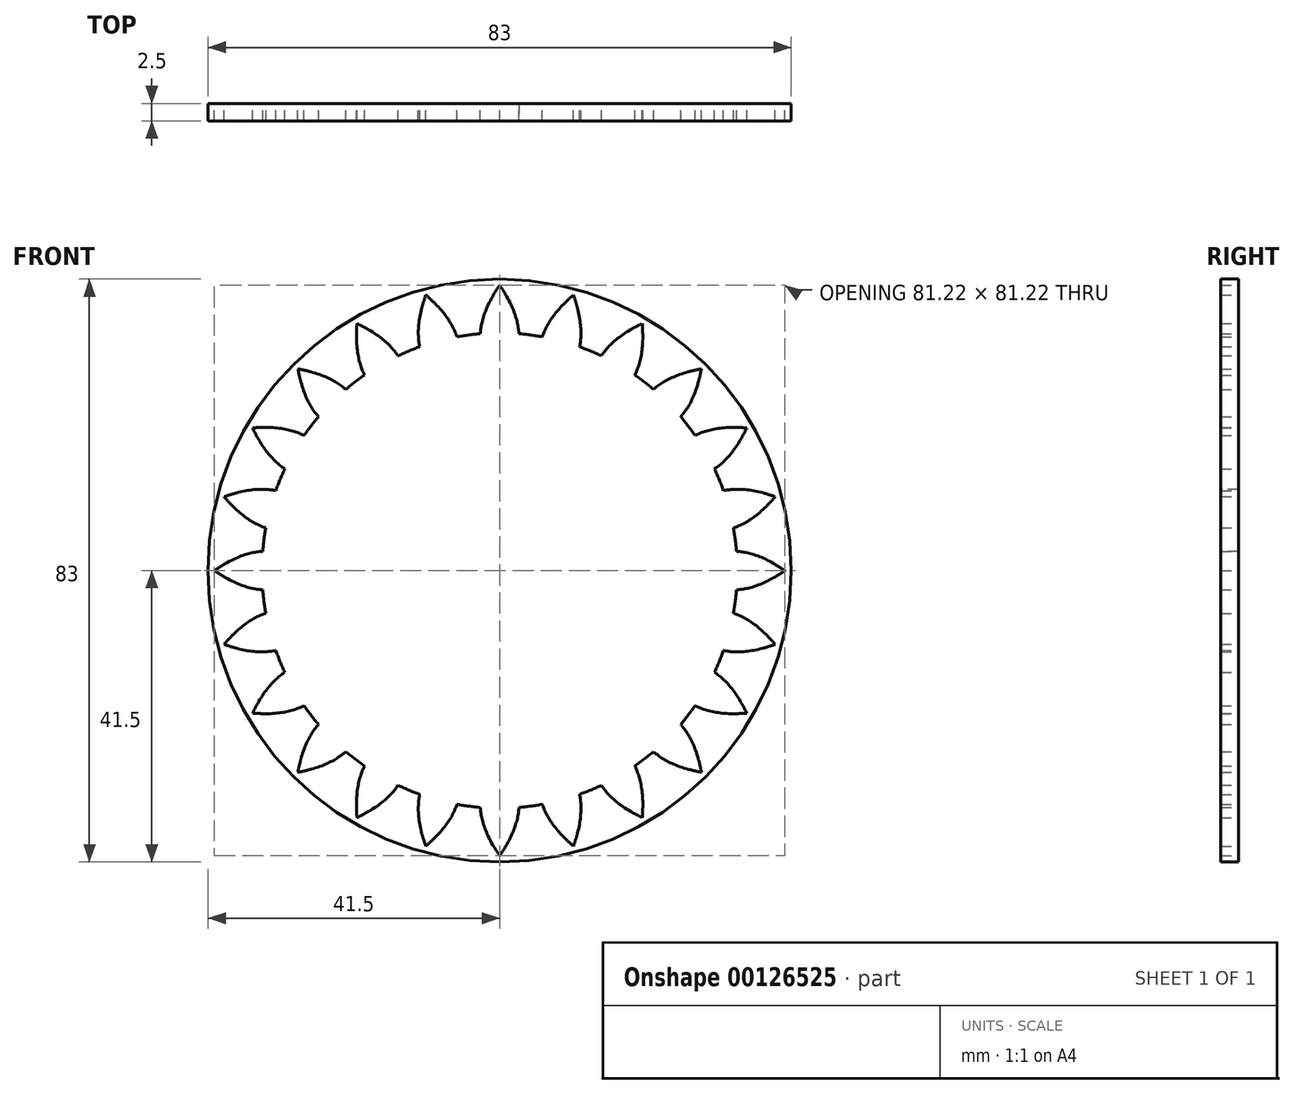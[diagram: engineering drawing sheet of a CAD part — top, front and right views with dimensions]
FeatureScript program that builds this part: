
annotation { "Feature Type Name" : "Feature", "Feature Type Description" : "" }
export const myFeature = defineFeature(function(context is Context, id is Id, definition is map)
    precondition{}
    {
        {
            assignVariable(context, id + "F0", {"name" : "NumberOfTeeth", "anyValue" : 24});
        }
        {
            var Q0;
            Q0=qCreatedBy(makeId("Front.planeOp"),FACE);
            var sketch = newSketch(context, id + "F1", { "sketchPlane" : qUnion([Q0])});
            skCircle(sketch, "E0", {"center": v(0, 0) * mm, "radius": 33.83 * mm});
            skCircle(sketch, "E1", {"center": v(0, 0) * mm, "radius": 39 * mm, "construction": true});
            skCircle(sketch, "E2", {"center": v(0, 0) * mm, "radius": 41.5 * mm});
            skSolve(sketch);
        }
        {
            var Q0;
            Q0=qSketchRegion(id+"F1",true);
            extrude(context, id + "F2", {"entities" : qUnion([Q0]), "depth" : 2.5 * mm});
        }
        {
            var Q0;
            Q0=qCreatedBy(makeId("Front.planeOp"),FACE);
            var sketch = newSketch(context, id + "F3", { "sketchPlane" : qUnion([Q0])});
            skCircle(sketch, "E3", {"center": v(0, 0) * mm, "radius": 36 * mm, "construction": true});
            skLineSegment(sketch, "E4", {"start": v(0, 0) * mm, "end": v(2.35, 35.92) * mm, "construction": true});
            skCircle(sketch, "E5.0", {"center": v(0, 0) * mm, "radius": 33.83 * mm, "construction": true});
            skLineSegment(sketch, "E6", {"start": v(0, 0) * mm, "end": v(4.7, 35.7) * mm, "construction": true});
            skLineSegment(sketch, "E7", {"start": v(0, 0) * mm, "end": v(2.74, 33.72) * mm, "construction": true});
            skLineSegment(sketch, "E8", {"start": v(0, 0) * mm, "end": v(-6.25, 33.25) * mm, "construction": true});
            skLineSegment(sketch, "E9", {"start": v(0, 0) * mm, "end": v(-14.8, 30.42) * mm, "construction": true});
            skLineSegment(sketch, "E10", {"start": v(0, 0) * mm, "end": v(-22.3, 25.45) * mm, "construction": true});
            skLineSegment(sketch, "E11", {"start": v(0, 0) * mm, "end": v(-28.21, 18.67) * mm, "construction": true});
            skLineSegment(sketch, "E12", {"start": v(2.74, 33.72) * mm, "end": v(-6.25, 33.25) * mm, "construction": true});
            skLineSegment(sketch, "E13", {"start": v(-6.25, 33.25) * mm, "end": v(-14.8, 30.42) * mm, "construction": true});
            skLineSegment(sketch, "E14", {"start": v(-14.8, 30.42) * mm, "end": v(-22.3, 25.45) * mm, "construction": true});
            skLineSegment(sketch, "E15", {"start": v(-22.3, 25.45) * mm, "end": v(-28.21, 18.67) * mm, "construction": true});
            skLineSegment(sketch, "E16", {"start": v(0, 0) * mm, "end": v(-32.14, 10.57) * mm, "construction": true});
            skLineSegment(sketch, "E17", {"start": v(-28.21, 18.67) * mm, "end": v(-32.14, 10.57) * mm, "construction": true});
            skLineSegment(sketch, "E18", {"start": v(-6.25, 33.25) * mm, "end": v(2.6, 34.9) * mm, "construction": true});
            skLineSegment(sketch, "E19", {"start": v(-14.8, 30.42) * mm, "end": v(1.4, 38.3) * mm, "construction": true});
            skLineSegment(sketch, "E20", {"start": v(-22.3, 25.45) * mm, "end": v(-1.98, 43.24) * mm, "construction": true});
            skLineSegment(sketch, "E21", {"start": v(-28.21, 18.67) * mm, "end": v(-8.34, 48.7) * mm, "construction": true});
            skLineSegment(sketch, "E22", {"start": v(-32.14, 10.57) * mm, "end": v(-18.08, 53.32) * mm, "construction": true});
            skCircle(sketch, "E23", {"center": v(0, 0) * mm, "radius": 39 * mm, "construction": true});
            skFitSpline(sketch, "E24", {"points": [v(2.74, 33.72) * mm, v(2.6, 34.9) * mm, v(1.4, 38.3) * mm, v(-1.98, 43.24) * mm, v(-8.34, 48.7) * mm, v(-18.08, 53.32) * mm], "startDerivative": vector(0.18, 3.1) * mm, "endDerivative": vector(-9.58, 5.23) * mm});
            skFitSpline(sketch, "E25.MirrorCS", {"points": [v(-2.74, 33.72) * mm, v(-2.6, 34.9) * mm, v(-1.4, 38.3) * mm, v(1.98, 43.24) * mm, v(8.34, 48.7) * mm, v(18.08, 53.32) * mm], "startDerivative": vector(-0.18, 3.1) * mm, "endDerivative": vector(9.58, 5.23) * mm});
            skLineSegment(sketch, "E26", {"start": v(-1.02, 38.99) * mm, "end": v(1, 39.04) * mm});
            skLineSegment(sketch, "E27", {"start": v(-2.74, 33.72) * mm, "end": v(0, 0) * mm});
            skLineSegment(sketch, "E28", {"start": v(2.74, 33.72) * mm, "end": v(0, 0) * mm});
            skSolve(sketch);
        }
        {
            var Q0;
            Q0=qSketchRegion(id+"F3",true);
            extrude(context, id + "F4", {"entities" : qUnion([Q0]), "depth" : 2.5 * mm});
        }
        {
            var Q0;
            Q0=makeQuery(id+"F4.opExtrude","SWEPT_BODY",BODY,{"disambiguationData":[OSD([sQuery(id+"F3.wireOp",EDGE,"E24"),sQuery(id+"F3.wireOp",EDGE,"E25.MirrorCS"),sQuery(id+"F3.wireOp",EDGE,"E26"),sQuery(id+"F3.wireOp",EDGE,"E27"),sQuery(id+"F3.wireOp",EDGE,"E28")])]});
            var Q1;
            Q1=sQuery(id+"F1.wireOp",EDGE,"E0");
            circularPattern(context, id + "F5", {"operationType" : NewBodyOperationType.REMOVE, "entities" : qUnion([Q0]), "axis" : qUnion([Q1]), "angle" : 360 * degree, "instanceCount" : round(getVariable(context, 'NumberOfTeeth')), "equalSpace" : true});
        }
        {
            var Q0;
            {var subQ0=makeQuery(id+"F4.opExtrude","CAP_FACE",FACE,{"disambiguationData":[OSD([sQuery(id+"F3.wireOp",EDGE,"1f885de5-3e7a-432a-b88a-3eaa30a7a401.0"),sQuery(id+"F3.wireOp",EDGE,"A7tLEwBN-HnOb-phWn-sB40-qaaEkIq7NDu9"),sQuery(id+"F3.wireOp",EDGE,"94f80f61-b426-4ec2-81a6-44f42ff73b0d"),sQuery(id+"F3.wireOp",EDGE,"3276b7df-17ce-42f5-8fef-bbce2681202d"),sQuery(id+"F3.wireOp",EDGE,"8cab6697-fc05-46dd-9d4d-494c43dbe1bc"),sQuery(id+"F3.wireOp",EDGE,"267e9553-86ea-40c7-a68d-067ff4e522c80.MirrorCS"),sQuery(id+"F3.wireOp",EDGE,"0081c8b5-e93b-4ec3-87cf-ae34b8c9de0e0.MirrorCS"),sQuery(id+"F3.wireOp",EDGE,"14eaaf62-2f47-4f70-a4e9-6a61db97f38f0.MirrorCS"),sQuery(id+"F3.wireOp",EDGE,"36c0f882-098c-494c-bc9e-4a3fa39534f60.MirrorCS")])],"isStart":false});Q0=makeQuery(id+"F5.boolean.opBoolean","MERGE",FACE,{"derivedFrom":[makeQuery(id+"F2.opExtrude","CAP_FACE",FACE,{"disambiguationData":[OSD([sQuery(id+"F1.wireOp",EDGE,"E0")])],"isStart":false}),subQ0,makeQuery(id+"F5.opPattern","COPY",FACE,{"derivedFrom":subQ0,"instanceName":"1"}),makeQuery(id+"F5.opPattern","COPY",FACE,{"derivedFrom":subQ0,"instanceName":"2"}),makeQuery(id+"F5.opPattern","COPY",FACE,{"derivedFrom":subQ0,"instanceName":"3"}),makeQuery(id+"F5.opPattern","COPY",FACE,{"derivedFrom":subQ0,"instanceName":"4"}),makeQuery(id+"F5.opPattern","COPY",FACE,{"derivedFrom":subQ0,"instanceName":"5"}),makeQuery(id+"F5.opPattern","COPY",FACE,{"derivedFrom":subQ0,"instanceName":"6"}),makeQuery(id+"F5.opPattern","COPY",FACE,{"derivedFrom":subQ0,"instanceName":"7"}),makeQuery(id+"F5.opPattern","COPY",FACE,{"derivedFrom":subQ0,"instanceName":"8"}),makeQuery(id+"F5.opPattern","COPY",FACE,{"derivedFrom":subQ0,"instanceName":"9"}),makeQuery(id+"F5.opPattern","COPY",FACE,{"derivedFrom":subQ0,"instanceName":"10"}),makeQuery(id+"F5.opPattern","COPY",FACE,{"derivedFrom":subQ0,"instanceName":"11"}),makeQuery(id+"F5.opPattern","COPY",FACE,{"derivedFrom":subQ0,"instanceName":"12"}),makeQuery(id+"F5.opPattern","COPY",FACE,{"derivedFrom":subQ0,"instanceName":"13"}),makeQuery(id+"F5.opPattern","COPY",FACE,{"derivedFrom":subQ0,"instanceName":"14"}),makeQuery(id+"F5.opPattern","COPY",FACE,{"derivedFrom":subQ0,"instanceName":"15"}),makeQuery(id+"F5.opPattern","COPY",FACE,{"derivedFrom":subQ0,"instanceName":"16"}),makeQuery(id+"F5.opPattern","COPY",FACE,{"derivedFrom":subQ0,"instanceName":"17"}),makeQuery(id+"F5.opPattern","COPY",FACE,{"derivedFrom":subQ0,"instanceName":"18"}),makeQuery(id+"F5.opPattern","COPY",FACE,{"derivedFrom":subQ0,"instanceName":"19"})]});}
            var sketch = newSketch(context, id + "F6", { "sketchPlane" : qUnion([Q0])});
            skCircle(sketch, "E29", {"center": v(0, 0) * mm, "radius": 1.5 * mm});
            skSolve(sketch);
        }
        {
            var Q0;
            Q0=qSketchRegion(id+"F6",true);
            extrude(context, id + "F7", {"entities" : qUnion([Q0]), "operationType" : NewBodyOperationType.REMOVE, "endBound" : BoundingType.THROUGH_ALL, "oppositeDirection" : true, "depth" : 25 * mm});
        }
    });
